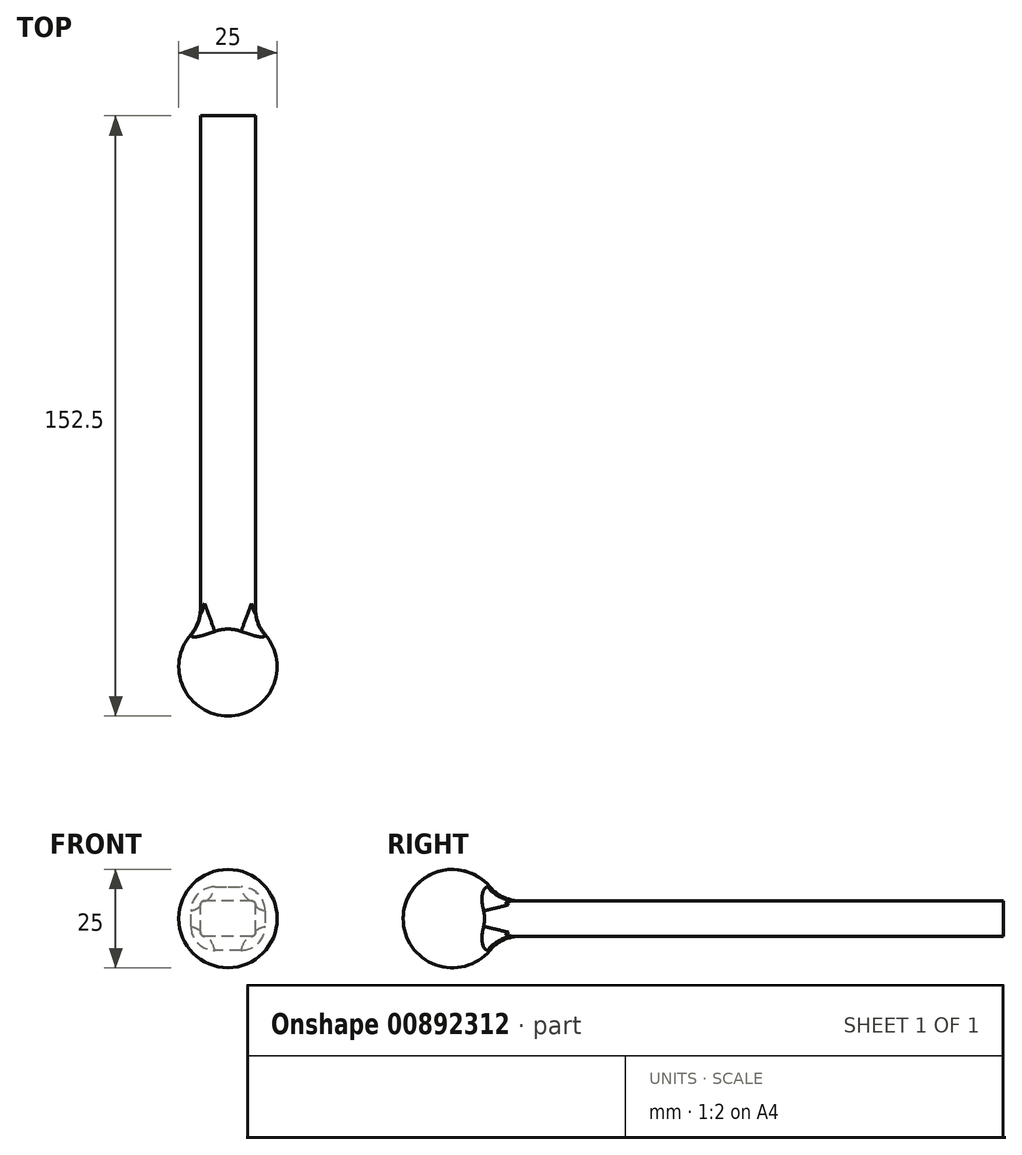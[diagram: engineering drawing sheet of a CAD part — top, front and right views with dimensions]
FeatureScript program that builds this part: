
annotation { "Feature Type Name" : "Feature", "Feature Type Description" : "" }
export const myFeature = defineFeature(function(context is Context, id is Id, definition is map)
    precondition{}
    {
        {
            var Q0;
            Q0=qCreatedBy(makeId("Front.planeOp"),FACE);
            var sketch = newSketch(context, id + "F0", { "sketchPlane" : qUnion([Q0])});
            skLineSegment(sketch, "E0.bottom", {"start": v(7, -4.5) * mm, "end": v(-7, -4.5) * mm});
            skLineSegment(sketch, "E0.top", {"start": v(7, 4.5) * mm, "end": v(-7, 4.5) * mm});
            skLineSegment(sketch, "E0.left", {"start": v(7, -4.5) * mm, "end": v(7, 4.5) * mm});
            skLineSegment(sketch, "E0.right", {"start": v(-7, -4.5) * mm, "end": v(-7, 4.5) * mm});
            skPoint(sketch, "E0.middle", {"position": v(0, 0) * mm});
            skSolve(sketch);
        }
        {
            var Q0;
            Q0=qSketchRegion(id+"F0",true);
            extrude(context, id + "F1", {"entities" : qUnion([Q0]), "oppositeDirection" : true, "depth" : 120 * mm});
        }
        {
            var Q0;
            Q0=makeQuery(id+"F0zmC9DmVHRgf0m_2.opLoft","SWEPT_EDGE",EDGE,{"disambiguationData":[OSD([sQuery(id+"F0.wireOp",EDGE,"E0.bottom"),sQuery(id+"F0.wireOp",EDGE,"E0.left"),sQuery(id+"Frc3L1yg7dYelYP_1.wireOp",EDGE,"BaSHiYCK-xsG4-pMvq-9rZi-0e0mhSe15c0g.top"),sQuery(id+"Frc3L1yg7dYelYP_1.wireOp",EDGE,"BaSHiYCK-xsG4-pMvq-9rZi-0e0mhSe15c0g.right")])]});
            var Q1;
            Q1=makeQuery(id+"F0zmC9DmVHRgf0m_2.opLoft","SWEPT_EDGE",EDGE,{"disambiguationData":[OSD([sQuery(id+"F0.wireOp",EDGE,"E0.bottom"),sQuery(id+"F0.wireOp",EDGE,"E0.right"),sQuery(id+"Frc3L1yg7dYelYP_1.wireOp",EDGE,"BaSHiYCK-xsG4-pMvq-9rZi-0e0mhSe15c0g.top"),sQuery(id+"Frc3L1yg7dYelYP_1.wireOp",EDGE,"BaSHiYCK-xsG4-pMvq-9rZi-0e0mhSe15c0g.right")])]});
            var Q2;
            Q2=makeQuery(id+"F0zmC9DmVHRgf0m_2.opLoft","SWEPT_EDGE",EDGE,{"disambiguationData":[OSD([sQuery(id+"F0.wireOp",EDGE,"E0.top"),sQuery(id+"F0.wireOp",EDGE,"E0.right"),sQuery(id+"Frc3L1yg7dYelYP_1.wireOp",EDGE,"BaSHiYCK-xsG4-pMvq-9rZi-0e0mhSe15c0g.bottom"),sQuery(id+"Frc3L1yg7dYelYP_1.wireOp",EDGE,"BaSHiYCK-xsG4-pMvq-9rZi-0e0mhSe15c0g.right")])]});
            var Q3;
            Q3=makeQuery(id+"F0zmC9DmVHRgf0m_2.opLoft","SWEPT_EDGE",EDGE,{"disambiguationData":[OSD([sQuery(id+"F0.wireOp",EDGE,"E0.top"),sQuery(id+"F0.wireOp",EDGE,"E0.left"),sQuery(id+"Frc3L1yg7dYelYP_1.wireOp",EDGE,"BaSHiYCK-xsG4-pMvq-9rZi-0e0mhSe15c0g.bottom"),sQuery(id+"Frc3L1yg7dYelYP_1.wireOp",EDGE,"BaSHiYCK-xsG4-pMvq-9rZi-0e0mhSe15c0g.right")])]});
            var Q4;
            Q4=makeQuery(id+"F1.opExtrude","SWEPT_EDGE",EDGE,{"disambiguationData":[OSD([sQuery(id+"F0.wireOp",EDGE,"E0.top"),sQuery(id+"F0.wireOp",EDGE,"E0.right")])]});
            var Q5;
            Q5=makeQuery(id+"F1.opExtrude","SWEPT_EDGE",EDGE,{"disambiguationData":[OSD([sQuery(id+"F0.wireOp",EDGE,"E0.bottom"),sQuery(id+"F0.wireOp",EDGE,"E0.right")])]});
            var Q6;
            Q6=makeQuery(id+"F1.opExtrude","SWEPT_EDGE",EDGE,{"disambiguationData":[OSD([sQuery(id+"F0.wireOp",EDGE,"E0.top"),sQuery(id+"F0.wireOp",EDGE,"E0.left")])]});
            var Q7;
            Q7=makeQuery(id+"F1.opExtrude","SWEPT_EDGE",EDGE,{"disambiguationData":[OSD([sQuery(id+"F0.wireOp",EDGE,"E0.bottom"),sQuery(id+"F0.wireOp",EDGE,"E0.left")])]});
            var Q8;
            Q8=makeQuery(id+"FnHOMDchlQBqzLB_1.opExtrude","CAP_EDGE",EDGE,{"disambiguationData":[OSD([sQuery(id+"Frc3L1yg7dYelYP_1.wireOp",EDGE,"BaSHiYCK-xsG4-pMvq-9rZi-0e0mhSe15c0g.top")])],"isStart":true});
            var Q9;
            Q9=makeQuery(id+"FnHOMDchlQBqzLB_1.opExtrude","CAP_EDGE",EDGE,{"disambiguationData":[OSD([sQuery(id+"Frc3L1yg7dYelYP_1.wireOp",EDGE,"BaSHiYCK-xsG4-pMvq-9rZi-0e0mhSe15c0g.top")])],"isStart":false});
            var Q10;
            Q10=makeQuery(id+"FnHOMDchlQBqzLB_1.opExtrude","CAP_EDGE",EDGE,{"disambiguationData":[OSD([sQuery(id+"Frc3L1yg7dYelYP_1.wireOp",EDGE,"BaSHiYCK-xsG4-pMvq-9rZi-0e0mhSe15c0g.bottom")])],"isStart":true});
            var Q11;
            Q11=makeQuery(id+"FnHOMDchlQBqzLB_1.opExtrude","CAP_EDGE",EDGE,{"disambiguationData":[OSD([sQuery(id+"Frc3L1yg7dYelYP_1.wireOp",EDGE,"BaSHiYCK-xsG4-pMvq-9rZi-0e0mhSe15c0g.bottom")])],"isStart":false});
            fillet(context, id + "F2", {"entities" : qUnion([Q0, Q1, Q2, Q3, Q4, Q5, Q6, Q7, Q8, Q9, Q10, Q11]), "radius" : 1 * mm, "tangentPropagation" : true, "allowEdgeOverflow" : false});
        }
        {
            var Q0;
            Q0=qCreatedBy(makeId("Right.planeOp"),FACE);
            var sketch = newSketch(context, id + "F3", { "sketchPlane" : qUnion([Q0])});
            skArc(sketch, "E1", {"start": v(-7.5, 0) * mm, "mid": v(-20, 12.5) * mm, "end": v(-32.5, 0) * mm});
            skLineSegment(sketch, "E2", {"start": v(-7.5, 0) * mm, "end": v(-32.5, 0) * mm});
            skSolve(sketch);
        }
        {
            var Q0;
            Q0=qCreatedBy(makeId("Right.planeOp"),FACE);
            var sketch = newSketch(context, id + "F4", { "sketchPlane" : qUnion([Q0])});
            skLineSegment(sketch, "E3", {"start": v(0, 0) * mm, "end": v(-19.2, 0) * mm});
            skSolve(sketch);
        }
        {
            var Q0;
            Q0=sQuery(id+"F3.wireOp",EDGE,"E1");
            var Q1;
            Q1=sQuery(id+"F4.wireOp",EDGE,"E3");
            revolve(context, id + "F5", {"bodyType" : ToolBodyType.SURFACE, "surfaceEntities" : qUnion([Q0]), "axis" : qUnion([Q1]), "revolveType" : RevolveType.FULL});
        }
        {
            var Q0;
            Q0=makeQuery(id+"F1.opExtrude","CAP_FACE",FACE,{"disambiguationData":[OSD([sQuery(id+"F0.wireOp",EDGE,"E0.bottom"),sQuery(id+"F0.wireOp",EDGE,"E0.top"),sQuery(id+"F0.wireOp",EDGE,"E0.left"),sQuery(id+"F0.wireOp",EDGE,"E0.right")])],"isStart":true});
            extrude(context, id + "F6", {"entities" : qUnion([Q0]), "operationType" : NewBodyOperationType.ADD, "depth" : 25 * mm, "hasSecondDirection" : true, "secondDirectionOppositeDirection" : true, "secondDirectionDepth" : 25 * mm});
        }
        {
            var Q0;
            Q0=qSketchRegion(id+"F3",true);
            var Q1;
            Q1=sQuery(id+"F4.wireOp",EDGE,"E3");
            revolve(context, id + "F7", {"operationType" : NewBodyOperationType.ADD, "entities" : qUnion([Q0]), "axis" : qUnion([Q1]), "revolveType" : RevolveType.FULL});
        }
        {
            var Q0;
            Q0=makeQuery(id+"F5.opRevolve","SWEPT_BODY",BODY,{"disambiguationData":[OSD([sQuery(id+"F3.wireOp",EDGE,"E1")])]});
            deleteBodies(context, id + "F8", {"entities" : qUnion([Q0])});
        }
        {
            var Q0;
            {var subQ0=sQuery(id+"F0.wireOp",EDGE,"E0.left");Q0=makeQuery(id+"F7.boolean.opBoolean","INTERSECT",EDGE,{"derivedFrom":[makeQuery(id+"F6.boolean.opBoolean","MERGE",FACE,{"derivedFrom":[makeQuery(id+"F1.opExtrude","SWEPT_FACE",FACE,{"disambiguationData":[OSD([subQ0])]}),makeQuery(id+"F6.opExtrude","SWEPT_FACE",FACE,{"disambiguationData":[OSD([subQ0])]})]}),makeQuery(id+"F7.opRevolve","SWEPT_FACE",FACE,{"disambiguationData":[OSD([sQuery(id+"F3.wireOp",EDGE,"E1")])]})]});}
            var Q1;
            {var subQ0=sQuery(id+"F0.wireOp",EDGE,"E0.bottom");Q1=makeQuery(id+"F7.boolean.opBoolean","INTERSECT",EDGE,{"derivedFrom":[makeQuery(id+"F6.boolean.opBoolean","MERGE",FACE,{"derivedFrom":[makeQuery(id+"F1.opExtrude","SWEPT_FACE",FACE,{"disambiguationData":[OSD([subQ0])]}),makeQuery(id+"F6.opExtrude","SWEPT_FACE",FACE,{"disambiguationData":[OSD([subQ0])]})]}),makeQuery(id+"F7.opRevolve","SWEPT_FACE",FACE,{"disambiguationData":[OSD([sQuery(id+"F3.wireOp",EDGE,"E1")])]})]});}
            var Q2;
            {var subQ0=sQuery(id+"F0.wireOp",EDGE,"E0.right");var subQ1=sQuery(id+"F0.wireOp",EDGE,"E0.left");var subQ2=sQuery(id+"F0.wireOp",EDGE,"E0.top");var subQ3=sQuery(id+"F0.wireOp",EDGE,"E0.bottom");Q2=makeQuery(id+"F7.boolean.opBoolean","INTERSECT",EDGE,{"derivedFrom":[makeQuery(id+"F6.boolean.opBoolean","MERGE",FACE,{"derivedFrom":[makeQuery(id+"F2.opFillet","BLEND_FACE",FACE,{"disambiguationData":[OSD([subQ3,subQ1])]}),makeQuery(id+"F6.opExtrude","SWEPT_FACE",FACE,{"disambiguationData":[OSD([subQ3,subQ2,subQ1,subQ0]),TDD([makeQuery(id+"F2.opFillet","BLEND_EDGE",EDGE,{"blendedFrom":[makeQuery(id+"F1.opExtrude","SWEPT_EDGE",EDGE,{"disambiguationData":[OSD([subQ3,subQ1])]}),makeQuery(id+"F1.opExtrude","CAP_FACE",FACE,{"disambiguationData":[OSD([subQ3,subQ2,subQ1,subQ0])],"isStart":true})],"blendedInto":[makeQuery(id+"F1.opExtrude","CAP_FACE",FACE,{"disambiguationData":[OSD([subQ3,subQ2,subQ1,subQ0])],"isStart":true})]})])]})]}),makeQuery(id+"F7.opRevolve","SWEPT_FACE",FACE,{"disambiguationData":[OSD([sQuery(id+"F3.wireOp",EDGE,"E1")])]})]});}
            fillet(context, id + "F9", {"entities" : qUnion([Q0, Q1, Q2]), "radius" : 10 * mm, "tangentPropagation" : true, "allowEdgeOverflow" : false});
        }
    });
